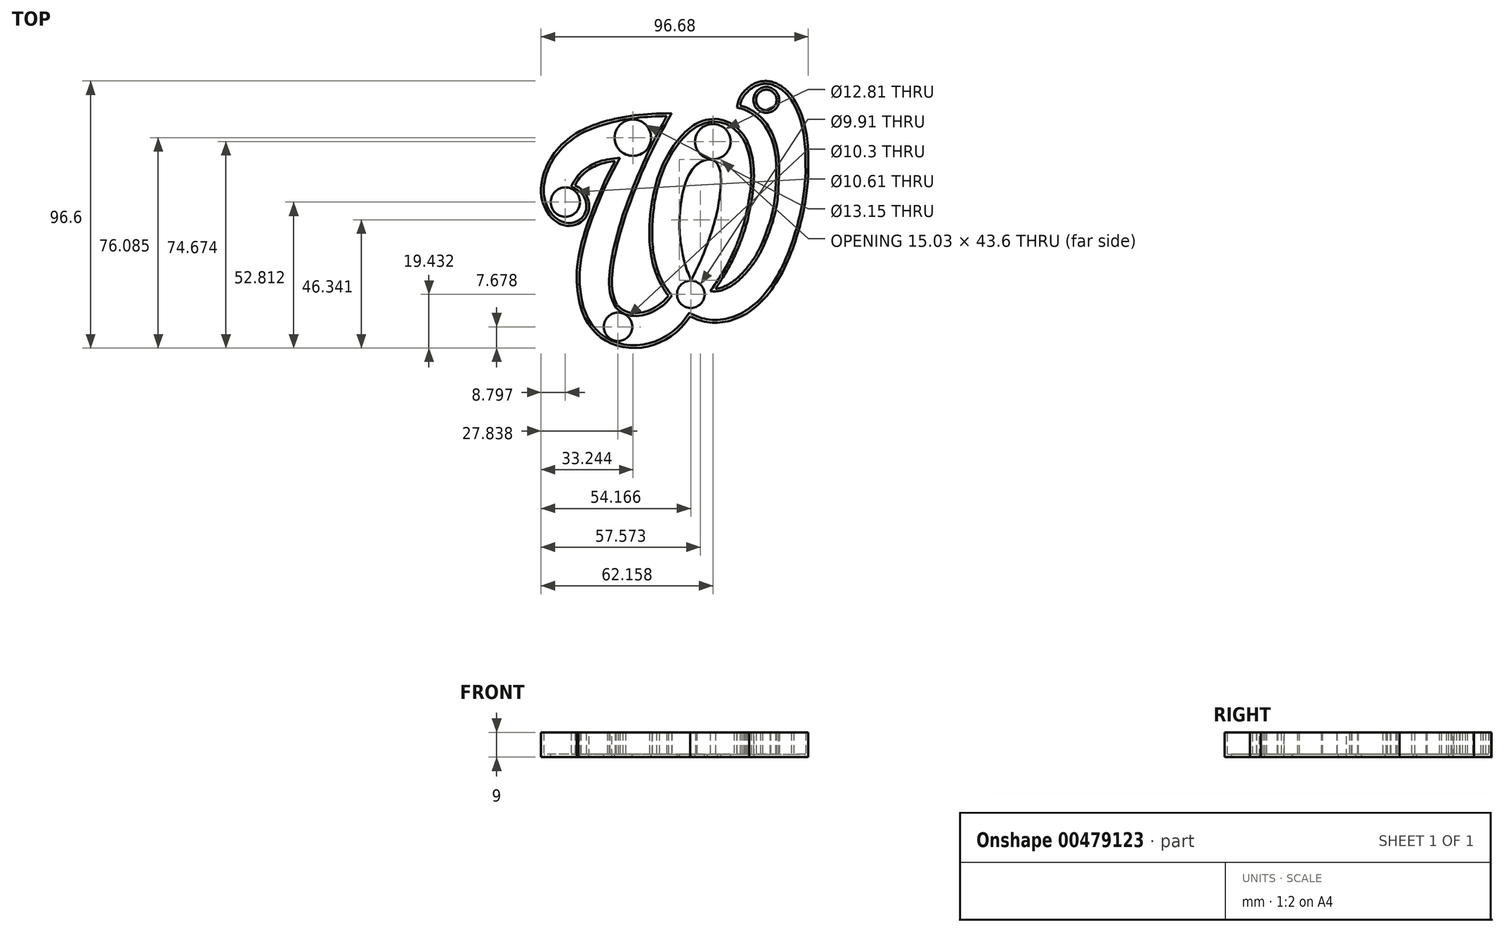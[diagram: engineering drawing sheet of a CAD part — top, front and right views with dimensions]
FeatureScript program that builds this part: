
annotation { "Feature Type Name" : "Feature", "Feature Type Description" : "" }
export const myFeature = defineFeature(function(context is Context, id is Id, definition is map)
    precondition{}
    {
        {
            var Q0;
            Q0=qCreatedBy(makeId("Top.planeOp"),FACE);
            var sketch = newSketch(context, id + "F0", { "sketchPlane" : qUnion([Q0])});
            skFitSpline(sketch, "E0", {"points": [v(-38.44, 13.04) * mm, v(-35.34, 0.5) * mm], "startDerivative": vector(19.27, -8.45) * mm, "endDerivative": vector(-8.88, -8.2) * mm});
            skFitSpline(sketch, "E1", {"points": [v(-35.34, 0.5) * mm, v(-50.32, 14.67) * mm], "startDerivative": vector(-21.62, -19.65) * mm, "endDerivative": vector(7.38, 33.62) * mm});
            skFitSpline(sketch, "E2", {"points": [v(-36.66, 32.65) * mm, v(-50.32, 14.67) * mm], "startDerivative": vector(-36.63, -20.96) * mm, "endDerivative": vector(-0.68, -3.07) * mm});
            skFitSpline(sketch, "E3", {"points": [v(-3.52, 39.1) * mm, v(-36.66, 32.65) * mm], "startDerivative": vector(-42.8, -0.12) * mm, "endDerivative": vector(-27.92, -13.6) * mm});
            skFitSpline(sketch, "E4", {"points": [v(-3.52, 39.1) * mm, v(-20.11, 2.2) * mm], "startDerivative": vector(-28.1, -51.8) * mm, "endDerivative": vector(-15.12, -41.3) * mm});
            skFitSpline(sketch, "E5", {"points": [v(-20.11, 2.2) * mm, v(-22.74, -30.6) * mm], "startDerivative": vector(-15.98, -51.16) * mm, "endDerivative": vector(11.91, -15.48) * mm});
            skFitSpline(sketch, "E6", {"points": [v(-22.74, -30.6) * mm, v(-4.6, -26.84) * mm], "startDerivative": vector(14.38, -15.94) * mm, "endDerivative": vector(11.9, 16.21) * mm});
            skFitSpline(sketch, "E7", {"points": [v(-4.6, -26.84) * mm, v(-11.49, -5.18) * mm], "startDerivative": vector(-14.06, 17.34) * mm, "endDerivative": vector(-0.4, 25.23) * mm});
            skFitSpline(sketch, "E8", {"points": [v(-8.9, 14.34) * mm, v(-11.49, -5.18) * mm], "startDerivative": vector(-7.14, -23.12) * mm, "endDerivative": vector(0.3, -10.23) * mm});
            skFitSpline(sketch, "E9", {"points": [v(5.16, 35.2) * mm, v(-8.9, 14.34) * mm], "startDerivative": vector(-12.95, -7.53) * mm, "endDerivative": vector(-9.06, -32.73) * mm});
            skFitSpline(sketch, "E10", {"points": [v(5.16, 35.2) * mm, v(24.55, 27.4) * mm], "startDerivative": vector(29.73, 16.27) * mm, "endDerivative": vector(5.54, -17.35) * mm});
            skFitSpline(sketch, "E11", {"points": [v(24.55, 27.4) * mm, v(23.9, 0) * mm], "startDerivative": vector(10, -26.88) * mm, "endDerivative": vector(-5.77, -24.7) * mm});
            skFitSpline(sketch, "E12", {"points": [v(23.9, 0) * mm, v(20.07, -10.82) * mm], "startDerivative": vector(-2.23, -7.81) * mm, "endDerivative": vector(-6.69, -15.42) * mm});
            skFitSpline(sketch, "E13", {"points": [v(12.38, -24.31) * mm, v(20.07, -10.82) * mm], "startDerivative": vector(7.85, 11.03) * mm, "endDerivative": vector(6.43, 15.26) * mm});
            skFitSpline(sketch, "E14", {"points": [v(12.38, -24.31) * mm, v(21.89, -18.84) * mm], "startDerivative": vector(9.06, -0.18) * mm, "endDerivative": vector(6.08, 7.24) * mm});
            skFitSpline(sketch, "E15", {"points": [v(29.24, -7.71) * mm, v(21.89, -18.84) * mm], "startDerivative": vector(-5.22, -12.66) * mm, "endDerivative": vector(-8.96, -9.02) * mm});
            skFitSpline(sketch, "E16", {"points": [v(34.12, 11.44) * mm, v(29.24, -7.71) * mm], "startDerivative": vector(-0.84, -23.2) * mm, "endDerivative": vector(-5.73, -13.72) * mm});
            skFitSpline(sketch, "E17", {"points": [v(28.71, 36.45) * mm, v(34.12, 11.44) * mm], "startDerivative": vector(20.5, -23.72) * mm, "endDerivative": vector(-1.25, -22.28) * mm});
            skFitSpline(sketch, "E18", {"points": [v(20.18, 41.18) * mm, v(28.71, 36.45) * mm], "startDerivative": vector(9.75, -2.02) * mm, "endDerivative": vector(8.86, -8.32) * mm});
            skFitSpline(sketch, "E19", {"points": [v(20.18, 41.18) * mm, v(23.25, 47.53) * mm], "startDerivative": vector(0.88, 6.3) * mm, "endDerivative": vector(7, 6.77) * mm});
            skFitSpline(sketch, "E20", {"points": [v(23.25, 47.53) * mm, v(32.34, 50.63) * mm], "startDerivative": vector(6.41, 6.4) * mm, "endDerivative": vector(12.36, -2.06) * mm});
            skFitSpline(sketch, "E21", {"points": [v(32.34, 50.63) * mm, v(40.68, 44.38) * mm], "startDerivative": vector(10.02, -2.32) * mm, "endDerivative": vector(5.39, -8.86) * mm});
            skFitSpline(sketch, "E22", {"points": [v(40.68, 44.38) * mm, v(45.99, 17.48) * mm], "startDerivative": vector(17.11, -26.78) * mm, "endDerivative": vector(0.17, -22.82) * mm});
            skFitSpline(sketch, "E23", {"points": [v(45.99, 17.48) * mm, v(42.24, -4.08) * mm], "startDerivative": vector(-1.45, -25.48) * mm, "endDerivative": vector(-5.86, -19.28) * mm});
            skFitSpline(sketch, "E24", {"points": [v(24.6, -32.7) * mm, v(42.24, -4.08) * mm], "startDerivative": vector(26.8, 18.38) * mm, "endDerivative": vector(10.07, 33.9) * mm});
            skFitSpline(sketch, "E25", {"points": [v(3.3, -34.32) * mm, v(24.6, -32.7) * mm], "startDerivative": vector(18.96, -10.38) * mm, "endDerivative": vector(22.17, 14.35) * mm});
            skFitSpline(sketch, "E26", {"points": [v(-37.26, -26.69) * mm, v(3.3, -34.32) * mm], "startDerivative": vector(9.1, -69.97) * mm, "endDerivative": vector(33.04, 50.98) * mm});
            skFitSpline(sketch, "E27", {"points": [v(-26.7, 16.54) * mm, v(-37.26, -26.69) * mm], "startDerivative": vector(-22.8, -49.62) * mm, "endDerivative": vector(6.72, -38.43) * mm});
            skFitSpline(sketch, "E28", {"points": [v(-23.93, 21.82) * mm, v(-26.7, 16.54) * mm], "startDerivative": vector(-2.78, -5.28) * mm, "endDerivative": vector(-2.78, -5.28) * mm});
            skFitSpline(sketch, "E29", {"points": [v(-38.44, 13.04) * mm, v(-23.93, 21.82) * mm], "startDerivative": vector(8.73, 17.34) * mm, "endDerivative": vector(18, 1.78) * mm});
            skFitSpline(sketch, "E30", {"points": [v(3.69, -18.9) * mm, v(12.08, 3.9) * mm], "startDerivative": vector(10.85, 21.47) * mm, "endDerivative": vector(5.7, 23.76) * mm});
            skFitSpline(sketch, "E31", {"points": [v(12.08, 3.9) * mm, v(9.54, 21.34) * mm], "startDerivative": vector(3.62, 18.83) * mm, "endDerivative": vector(-17.05, -2.6) * mm});
            skFitSpline(sketch, "E32", {"points": [v(0.44, -4.54) * mm, v(9.54, 21.34) * mm], "startDerivative": vector(-1.31, 24.15) * mm, "endDerivative": vector(24.76, 4.23) * mm});
            skFitSpline(sketch, "E33", {"points": [v(0.44, -4.54) * mm, v(3.69, -18.9) * mm], "startDerivative": vector(2.09, -17.75) * mm, "endDerivative": vector(5.24, -12.14) * mm});
            skCircle(sketch, "E34", {"center": v(-17.45, 30.27) * mm, "radius": 5.58 * mm});
            skCircle(sketch, "E35", {"center": v(-41.9, 7) * mm, "radius": 4.3 * mm});
            skCircle(sketch, "E36", {"center": v(-22.85, -38.13) * mm, "radius": 4.15 * mm});
            skCircle(sketch, "E37", {"center": v(3.48, -26.38) * mm, "radius": 3.96 * mm});
            skCircle(sketch, "E38", {"center": v(11.47, 28.86) * mm, "radius": 5.4 * mm});
            skCircle(sketch, "E39", {"center": v(30.8, 43.96) * mm, "radius": 3.69 * mm});
            skSolve(sketch);
        }
        {
            var Q0;
            Q0=makeQuery(id+"F0.imprint","IMPRINT",FACE,{"disambiguationData":[TD([[makeQuery(id+"F0.imprint","IMPRINT",EDGE,{"derivedFrom":sQuery(id+"F0.wireOp",EDGE,"E0")}),-1.0]])]});
            extrude(context, id + "F1", {"entities" : qUnion([Q0]), "depth" : 9 * mm});
        }
        {
            var Q0;
            Q0=makeQuery(id+"F1.opExtrude","CAP_FACE",FACE,{"disambiguationData":[OSD([sQuery(id+"F0.wireOp",EDGE,"E0"),sQuery(id+"F0.wireOp",EDGE,"E1"),sQuery(id+"F0.wireOp",EDGE,"E2"),sQuery(id+"F0.wireOp",EDGE,"E3"),sQuery(id+"F0.wireOp",EDGE,"E4"),sQuery(id+"F0.wireOp",EDGE,"E5"),sQuery(id+"F0.wireOp",EDGE,"E6"),sQuery(id+"F0.wireOp",EDGE,"E7"),sQuery(id+"F0.wireOp",EDGE,"E8"),sQuery(id+"F0.wireOp",EDGE,"E9"),sQuery(id+"F0.wireOp",EDGE,"E10"),sQuery(id+"F0.wireOp",EDGE,"E11"),sQuery(id+"F0.wireOp",EDGE,"E12"),sQuery(id+"F0.wireOp",EDGE,"E13"),sQuery(id+"F0.wireOp",EDGE,"E14"),sQuery(id+"F0.wireOp",EDGE,"E15"),sQuery(id+"F0.wireOp",EDGE,"E16"),sQuery(id+"F0.wireOp",EDGE,"E17"),sQuery(id+"F0.wireOp",EDGE,"E18"),sQuery(id+"F0.wireOp",EDGE,"E19"),sQuery(id+"F0.wireOp",EDGE,"E20"),sQuery(id+"F0.wireOp",EDGE,"E21"),sQuery(id+"F0.wireOp",EDGE,"E22"),sQuery(id+"F0.wireOp",EDGE,"E23"),sQuery(id+"F0.wireOp",EDGE,"E24"),sQuery(id+"F0.wireOp",EDGE,"E25"),sQuery(id+"F0.wireOp",EDGE,"E26"),sQuery(id+"F0.wireOp",EDGE,"E27"),sQuery(id+"F0.wireOp",EDGE,"E28"),sQuery(id+"F0.wireOp",EDGE,"E29"),sQuery(id+"F0.wireOp",EDGE,"E30"),sQuery(id+"F0.wireOp",EDGE,"E31"),sQuery(id+"F0.wireOp",EDGE,"E32"),sQuery(id+"F0.wireOp",EDGE,"E33"),sQuery(id+"F0.wireOp",EDGE,"T4ResZmE-MT7P-ZZB1-tC4J-8hycNHcue7vr"),sQuery(id+"F0.wireOp",EDGE,"OMnXbtUw-R1gw-jA70-7ST3-ESDXTdVTGBNz"),sQuery(id+"F0.wireOp",EDGE,"2kX4wL51-abr2-e3rj-M2hi-KkItlir6IYqc"),sQuery(id+"F0.wireOp",EDGE,"5Vguvqgd-1i0I-IiD5-Ilya-cWlO0dk4ybGS"),sQuery(id+"F0.wireOp",EDGE,"b57bD0nZ-s6Al-luj6-F2sP-Uw2OASkc7xh6"),sQuery(id+"F0.wireOp",EDGE,"YTZRzNyw-rSVb-fAv7-5o0Q-GydmuSaNebT5"),sQuery(id+"F0.wireOp",EDGE,"wcS51u0E-04dH-7dC1-kLtU-daWTJbN2IP2I")])],"isStart":false});
            shell(context, id + "F2", {"entities" : qUnion([Q0]), "thickness" : 1 * mm});
        }
        {
            var Q0;
            {var subQ0=sQuery(id+"F0.wireOp",EDGE,"E39");var subQ1=sQuery(id+"F0.wireOp",EDGE,"E38");var subQ2=sQuery(id+"F0.wireOp",EDGE,"E37");var subQ3=sQuery(id+"F0.wireOp",EDGE,"E36");var subQ4=sQuery(id+"F0.wireOp",EDGE,"E35");var subQ5=sQuery(id+"F0.wireOp",EDGE,"E34");var subQ6=sQuery(id+"F0.wireOp",EDGE,"E33");var subQ7=sQuery(id+"F0.wireOp",EDGE,"E32");var subQ8=sQuery(id+"F0.wireOp",EDGE,"E31");var subQ9=sQuery(id+"F0.wireOp",EDGE,"E30");var subQ10=sQuery(id+"F0.wireOp",EDGE,"E29");var subQ11=sQuery(id+"F0.wireOp",EDGE,"E28");var subQ12=sQuery(id+"F0.wireOp",EDGE,"E27");var subQ13=sQuery(id+"F0.wireOp",EDGE,"E26");var subQ14=sQuery(id+"F0.wireOp",EDGE,"E25");var subQ15=sQuery(id+"F0.wireOp",EDGE,"E24");var subQ16=sQuery(id+"F0.wireOp",EDGE,"E23");var subQ17=sQuery(id+"F0.wireOp",EDGE,"E22");var subQ18=sQuery(id+"F0.wireOp",EDGE,"E21");var subQ19=sQuery(id+"F0.wireOp",EDGE,"E20");var subQ20=sQuery(id+"F0.wireOp",EDGE,"E19");var subQ21=sQuery(id+"F0.wireOp",EDGE,"E18");var subQ22=sQuery(id+"F0.wireOp",EDGE,"E17");var subQ23=sQuery(id+"F0.wireOp",EDGE,"E16");var subQ24=sQuery(id+"F0.wireOp",EDGE,"E15");var subQ25=sQuery(id+"F0.wireOp",EDGE,"E14");var subQ26=sQuery(id+"F0.wireOp",EDGE,"E13");var subQ27=sQuery(id+"F0.wireOp",EDGE,"E12");var subQ28=sQuery(id+"F0.wireOp",EDGE,"E11");var subQ29=sQuery(id+"F0.wireOp",EDGE,"E10");var subQ30=sQuery(id+"F0.wireOp",EDGE,"E9");var subQ31=sQuery(id+"F0.wireOp",EDGE,"E8");var subQ32=sQuery(id+"F0.wireOp",EDGE,"E7");var subQ33=sQuery(id+"F0.wireOp",EDGE,"E6");var subQ34=sQuery(id+"F0.wireOp",EDGE,"E5");var subQ35=sQuery(id+"F0.wireOp",EDGE,"E4");var subQ36=sQuery(id+"F0.wireOp",EDGE,"E3");var subQ37=sQuery(id+"F0.wireOp",EDGE,"E2");var subQ38=sQuery(id+"F0.wireOp",EDGE,"E1");var subQ39=sQuery(id+"F0.wireOp",EDGE,"E0");Q0=makeQuery(id+"F2.opShell","OFFSET_FACE",FACE,{"disambiguationData":[OSD([subQ39,subQ38,subQ37,subQ36,subQ35,subQ34,subQ33,subQ32,subQ31,subQ30,subQ29,subQ28,subQ27,subQ26,subQ25,subQ24,subQ23,subQ22,subQ21,subQ20,subQ19,subQ18,subQ17,subQ16,subQ15,subQ14,subQ13,subQ12,subQ11,subQ10,subQ9,subQ8,subQ7,subQ6,subQ5,subQ4,subQ3,subQ2,subQ1,subQ0]),TDD([makeQuery(id+"F1.opExtrude","CAP_FACE",FACE,{"disambiguationData":[OSD([subQ39,subQ38,subQ37,subQ36,subQ35,subQ34,subQ33,subQ32,subQ31,subQ30,subQ29,subQ28,subQ27,subQ26,subQ25,subQ24,subQ23,subQ22,subQ21,subQ20,subQ19,subQ18,subQ17,subQ16,subQ15,subQ14,subQ13,subQ12,subQ11,subQ10,subQ9,subQ8,subQ7,subQ6,subQ5,subQ4,subQ3,subQ2,subQ1,subQ0])],"isStart":false})]),OD(1.0)]});}
            var Q1;
            {var subQ0=sQuery(id+"F0.wireOp",EDGE,"E39");var subQ1=sQuery(id+"F0.wireOp",EDGE,"E38");var subQ2=sQuery(id+"F0.wireOp",EDGE,"E37");var subQ3=sQuery(id+"F0.wireOp",EDGE,"E36");var subQ4=sQuery(id+"F0.wireOp",EDGE,"E35");var subQ5=sQuery(id+"F0.wireOp",EDGE,"E34");var subQ6=sQuery(id+"F0.wireOp",EDGE,"E33");var subQ7=sQuery(id+"F0.wireOp",EDGE,"E32");var subQ8=sQuery(id+"F0.wireOp",EDGE,"E31");var subQ9=sQuery(id+"F0.wireOp",EDGE,"E30");var subQ10=sQuery(id+"F0.wireOp",EDGE,"E29");var subQ11=sQuery(id+"F0.wireOp",EDGE,"E28");var subQ12=sQuery(id+"F0.wireOp",EDGE,"E27");var subQ13=sQuery(id+"F0.wireOp",EDGE,"E26");var subQ14=sQuery(id+"F0.wireOp",EDGE,"E25");var subQ15=sQuery(id+"F0.wireOp",EDGE,"E24");var subQ16=sQuery(id+"F0.wireOp",EDGE,"E23");var subQ17=sQuery(id+"F0.wireOp",EDGE,"E22");var subQ18=sQuery(id+"F0.wireOp",EDGE,"E21");var subQ19=sQuery(id+"F0.wireOp",EDGE,"E20");var subQ20=sQuery(id+"F0.wireOp",EDGE,"E19");var subQ21=sQuery(id+"F0.wireOp",EDGE,"E18");var subQ22=sQuery(id+"F0.wireOp",EDGE,"E17");var subQ23=sQuery(id+"F0.wireOp",EDGE,"E16");var subQ24=sQuery(id+"F0.wireOp",EDGE,"E15");var subQ25=sQuery(id+"F0.wireOp",EDGE,"E14");var subQ26=sQuery(id+"F0.wireOp",EDGE,"E13");var subQ27=sQuery(id+"F0.wireOp",EDGE,"E12");var subQ28=sQuery(id+"F0.wireOp",EDGE,"E11");var subQ29=sQuery(id+"F0.wireOp",EDGE,"E10");var subQ30=sQuery(id+"F0.wireOp",EDGE,"E9");var subQ31=sQuery(id+"F0.wireOp",EDGE,"E8");var subQ32=sQuery(id+"F0.wireOp",EDGE,"E7");var subQ33=sQuery(id+"F0.wireOp",EDGE,"E6");var subQ34=sQuery(id+"F0.wireOp",EDGE,"E5");var subQ35=sQuery(id+"F0.wireOp",EDGE,"E4");var subQ36=sQuery(id+"F0.wireOp",EDGE,"E3");var subQ37=sQuery(id+"F0.wireOp",EDGE,"E2");var subQ38=sQuery(id+"F0.wireOp",EDGE,"E1");var subQ39=sQuery(id+"F0.wireOp",EDGE,"E0");Q1=makeQuery(id+"F2.opShell","OFFSET_FACE",FACE,{"disambiguationData":[OSD([subQ39,subQ38,subQ37,subQ36,subQ35,subQ34,subQ33,subQ32,subQ31,subQ30,subQ29,subQ28,subQ27,subQ26,subQ25,subQ24,subQ23,subQ22,subQ21,subQ20,subQ19,subQ18,subQ17,subQ16,subQ15,subQ14,subQ13,subQ12,subQ11,subQ10,subQ9,subQ8,subQ7,subQ6,subQ5,subQ4,subQ3,subQ2,subQ1,subQ0]),TDD([makeQuery(id+"F1.opExtrude","CAP_FACE",FACE,{"disambiguationData":[OSD([subQ39,subQ38,subQ37,subQ36,subQ35,subQ34,subQ33,subQ32,subQ31,subQ30,subQ29,subQ28,subQ27,subQ26,subQ25,subQ24,subQ23,subQ22,subQ21,subQ20,subQ19,subQ18,subQ17,subQ16,subQ15,subQ14,subQ13,subQ12,subQ11,subQ10,subQ9,subQ8,subQ7,subQ6,subQ5,subQ4,subQ3,subQ2,subQ1,subQ0])],"isStart":false})]),OD(2.0)]});}
            var Q2;
            {var subQ0=sQuery(id+"F0.wireOp",EDGE,"E39");var subQ1=sQuery(id+"F0.wireOp",EDGE,"E38");var subQ2=sQuery(id+"F0.wireOp",EDGE,"E37");var subQ3=sQuery(id+"F0.wireOp",EDGE,"E36");var subQ4=sQuery(id+"F0.wireOp",EDGE,"E35");var subQ5=sQuery(id+"F0.wireOp",EDGE,"E34");var subQ6=sQuery(id+"F0.wireOp",EDGE,"E33");var subQ7=sQuery(id+"F0.wireOp",EDGE,"E32");var subQ8=sQuery(id+"F0.wireOp",EDGE,"E31");var subQ9=sQuery(id+"F0.wireOp",EDGE,"E30");var subQ10=sQuery(id+"F0.wireOp",EDGE,"E29");var subQ11=sQuery(id+"F0.wireOp",EDGE,"E28");var subQ12=sQuery(id+"F0.wireOp",EDGE,"E27");var subQ13=sQuery(id+"F0.wireOp",EDGE,"E26");var subQ14=sQuery(id+"F0.wireOp",EDGE,"E25");var subQ15=sQuery(id+"F0.wireOp",EDGE,"E24");var subQ16=sQuery(id+"F0.wireOp",EDGE,"E23");var subQ17=sQuery(id+"F0.wireOp",EDGE,"E22");var subQ18=sQuery(id+"F0.wireOp",EDGE,"E21");var subQ19=sQuery(id+"F0.wireOp",EDGE,"E20");var subQ20=sQuery(id+"F0.wireOp",EDGE,"E19");var subQ21=sQuery(id+"F0.wireOp",EDGE,"E18");var subQ22=sQuery(id+"F0.wireOp",EDGE,"E17");var subQ23=sQuery(id+"F0.wireOp",EDGE,"E16");var subQ24=sQuery(id+"F0.wireOp",EDGE,"E15");var subQ25=sQuery(id+"F0.wireOp",EDGE,"E14");var subQ26=sQuery(id+"F0.wireOp",EDGE,"E13");var subQ27=sQuery(id+"F0.wireOp",EDGE,"E12");var subQ28=sQuery(id+"F0.wireOp",EDGE,"E11");var subQ29=sQuery(id+"F0.wireOp",EDGE,"E10");var subQ30=sQuery(id+"F0.wireOp",EDGE,"E9");var subQ31=sQuery(id+"F0.wireOp",EDGE,"E8");var subQ32=sQuery(id+"F0.wireOp",EDGE,"E7");var subQ33=sQuery(id+"F0.wireOp",EDGE,"E6");var subQ34=sQuery(id+"F0.wireOp",EDGE,"E5");var subQ35=sQuery(id+"F0.wireOp",EDGE,"E4");var subQ36=sQuery(id+"F0.wireOp",EDGE,"E3");var subQ37=sQuery(id+"F0.wireOp",EDGE,"E2");var subQ38=sQuery(id+"F0.wireOp",EDGE,"E1");var subQ39=sQuery(id+"F0.wireOp",EDGE,"E0");Q2=makeQuery(id+"F2.opShell","OFFSET_FACE",FACE,{"disambiguationData":[OSD([subQ39,subQ38,subQ37,subQ36,subQ35,subQ34,subQ33,subQ32,subQ31,subQ30,subQ29,subQ28,subQ27,subQ26,subQ25,subQ24,subQ23,subQ22,subQ21,subQ20,subQ19,subQ18,subQ17,subQ16,subQ15,subQ14,subQ13,subQ12,subQ11,subQ10,subQ9,subQ8,subQ7,subQ6,subQ5,subQ4,subQ3,subQ2,subQ1,subQ0]),TDD([makeQuery(id+"F1.opExtrude","CAP_FACE",FACE,{"disambiguationData":[OSD([subQ39,subQ38,subQ37,subQ36,subQ35,subQ34,subQ33,subQ32,subQ31,subQ30,subQ29,subQ28,subQ27,subQ26,subQ25,subQ24,subQ23,subQ22,subQ21,subQ20,subQ19,subQ18,subQ17,subQ16,subQ15,subQ14,subQ13,subQ12,subQ11,subQ10,subQ9,subQ8,subQ7,subQ6,subQ5,subQ4,subQ3,subQ2,subQ1,subQ0])],"isStart":false})]),OD(3.0)]});}
            var Q3;
            {var subQ0=sQuery(id+"F0.wireOp",EDGE,"E39");var subQ1=sQuery(id+"F0.wireOp",EDGE,"E38");var subQ2=sQuery(id+"F0.wireOp",EDGE,"E37");var subQ3=sQuery(id+"F0.wireOp",EDGE,"E36");var subQ4=sQuery(id+"F0.wireOp",EDGE,"E35");var subQ5=sQuery(id+"F0.wireOp",EDGE,"E34");var subQ6=sQuery(id+"F0.wireOp",EDGE,"E33");var subQ7=sQuery(id+"F0.wireOp",EDGE,"E32");var subQ8=sQuery(id+"F0.wireOp",EDGE,"E31");var subQ9=sQuery(id+"F0.wireOp",EDGE,"E30");var subQ10=sQuery(id+"F0.wireOp",EDGE,"E29");var subQ11=sQuery(id+"F0.wireOp",EDGE,"E28");var subQ12=sQuery(id+"F0.wireOp",EDGE,"E27");var subQ13=sQuery(id+"F0.wireOp",EDGE,"E26");var subQ14=sQuery(id+"F0.wireOp",EDGE,"E25");var subQ15=sQuery(id+"F0.wireOp",EDGE,"E24");var subQ16=sQuery(id+"F0.wireOp",EDGE,"E23");var subQ17=sQuery(id+"F0.wireOp",EDGE,"E22");var subQ18=sQuery(id+"F0.wireOp",EDGE,"E21");var subQ19=sQuery(id+"F0.wireOp",EDGE,"E20");var subQ20=sQuery(id+"F0.wireOp",EDGE,"E19");var subQ21=sQuery(id+"F0.wireOp",EDGE,"E18");var subQ22=sQuery(id+"F0.wireOp",EDGE,"E17");var subQ23=sQuery(id+"F0.wireOp",EDGE,"E16");var subQ24=sQuery(id+"F0.wireOp",EDGE,"E15");var subQ25=sQuery(id+"F0.wireOp",EDGE,"E14");var subQ26=sQuery(id+"F0.wireOp",EDGE,"E13");var subQ27=sQuery(id+"F0.wireOp",EDGE,"E12");var subQ28=sQuery(id+"F0.wireOp",EDGE,"E11");var subQ29=sQuery(id+"F0.wireOp",EDGE,"E10");var subQ30=sQuery(id+"F0.wireOp",EDGE,"E9");var subQ31=sQuery(id+"F0.wireOp",EDGE,"E8");var subQ32=sQuery(id+"F0.wireOp",EDGE,"E7");var subQ33=sQuery(id+"F0.wireOp",EDGE,"E6");var subQ34=sQuery(id+"F0.wireOp",EDGE,"E5");var subQ35=sQuery(id+"F0.wireOp",EDGE,"E4");var subQ36=sQuery(id+"F0.wireOp",EDGE,"E3");var subQ37=sQuery(id+"F0.wireOp",EDGE,"E2");var subQ38=sQuery(id+"F0.wireOp",EDGE,"E1");var subQ39=sQuery(id+"F0.wireOp",EDGE,"E0");Q3=makeQuery(id+"F2.opShell","OFFSET_FACE",FACE,{"disambiguationData":[OSD([subQ39,subQ38,subQ37,subQ36,subQ35,subQ34,subQ33,subQ32,subQ31,subQ30,subQ29,subQ28,subQ27,subQ26,subQ25,subQ24,subQ23,subQ22,subQ21,subQ20,subQ19,subQ18,subQ17,subQ16,subQ15,subQ14,subQ13,subQ12,subQ11,subQ10,subQ9,subQ8,subQ7,subQ6,subQ5,subQ4,subQ3,subQ2,subQ1,subQ0]),TDD([makeQuery(id+"F1.opExtrude","CAP_FACE",FACE,{"disambiguationData":[OSD([subQ39,subQ38,subQ37,subQ36,subQ35,subQ34,subQ33,subQ32,subQ31,subQ30,subQ29,subQ28,subQ27,subQ26,subQ25,subQ24,subQ23,subQ22,subQ21,subQ20,subQ19,subQ18,subQ17,subQ16,subQ15,subQ14,subQ13,subQ12,subQ11,subQ10,subQ9,subQ8,subQ7,subQ6,subQ5,subQ4,subQ3,subQ2,subQ1,subQ0])],"isStart":false})]),OD(4.0)]});}
            var Q4;
            {var subQ0=sQuery(id+"F0.wireOp",EDGE,"E39");var subQ1=sQuery(id+"F0.wireOp",EDGE,"E38");var subQ2=sQuery(id+"F0.wireOp",EDGE,"E37");var subQ3=sQuery(id+"F0.wireOp",EDGE,"E36");var subQ4=sQuery(id+"F0.wireOp",EDGE,"E35");var subQ5=sQuery(id+"F0.wireOp",EDGE,"E34");var subQ6=sQuery(id+"F0.wireOp",EDGE,"E33");var subQ7=sQuery(id+"F0.wireOp",EDGE,"E32");var subQ8=sQuery(id+"F0.wireOp",EDGE,"E31");var subQ9=sQuery(id+"F0.wireOp",EDGE,"E30");var subQ10=sQuery(id+"F0.wireOp",EDGE,"E29");var subQ11=sQuery(id+"F0.wireOp",EDGE,"E28");var subQ12=sQuery(id+"F0.wireOp",EDGE,"E27");var subQ13=sQuery(id+"F0.wireOp",EDGE,"E26");var subQ14=sQuery(id+"F0.wireOp",EDGE,"E25");var subQ15=sQuery(id+"F0.wireOp",EDGE,"E24");var subQ16=sQuery(id+"F0.wireOp",EDGE,"E23");var subQ17=sQuery(id+"F0.wireOp",EDGE,"E22");var subQ18=sQuery(id+"F0.wireOp",EDGE,"E21");var subQ19=sQuery(id+"F0.wireOp",EDGE,"E20");var subQ20=sQuery(id+"F0.wireOp",EDGE,"E19");var subQ21=sQuery(id+"F0.wireOp",EDGE,"E18");var subQ22=sQuery(id+"F0.wireOp",EDGE,"E17");var subQ23=sQuery(id+"F0.wireOp",EDGE,"E16");var subQ24=sQuery(id+"F0.wireOp",EDGE,"E15");var subQ25=sQuery(id+"F0.wireOp",EDGE,"E14");var subQ26=sQuery(id+"F0.wireOp",EDGE,"E13");var subQ27=sQuery(id+"F0.wireOp",EDGE,"E12");var subQ28=sQuery(id+"F0.wireOp",EDGE,"E11");var subQ29=sQuery(id+"F0.wireOp",EDGE,"E10");var subQ30=sQuery(id+"F0.wireOp",EDGE,"E9");var subQ31=sQuery(id+"F0.wireOp",EDGE,"E8");var subQ32=sQuery(id+"F0.wireOp",EDGE,"E7");var subQ33=sQuery(id+"F0.wireOp",EDGE,"E6");var subQ34=sQuery(id+"F0.wireOp",EDGE,"E5");var subQ35=sQuery(id+"F0.wireOp",EDGE,"E4");var subQ36=sQuery(id+"F0.wireOp",EDGE,"E3");var subQ37=sQuery(id+"F0.wireOp",EDGE,"E2");var subQ38=sQuery(id+"F0.wireOp",EDGE,"E1");var subQ39=sQuery(id+"F0.wireOp",EDGE,"E0");Q4=makeQuery(id+"F2.opShell","OFFSET_FACE",FACE,{"disambiguationData":[OSD([subQ39,subQ38,subQ37,subQ36,subQ35,subQ34,subQ33,subQ32,subQ31,subQ30,subQ29,subQ28,subQ27,subQ26,subQ25,subQ24,subQ23,subQ22,subQ21,subQ20,subQ19,subQ18,subQ17,subQ16,subQ15,subQ14,subQ13,subQ12,subQ11,subQ10,subQ9,subQ8,subQ7,subQ6,subQ5,subQ4,subQ3,subQ2,subQ1,subQ0]),TDD([makeQuery(id+"F1.opExtrude","CAP_FACE",FACE,{"disambiguationData":[OSD([subQ39,subQ38,subQ37,subQ36,subQ35,subQ34,subQ33,subQ32,subQ31,subQ30,subQ29,subQ28,subQ27,subQ26,subQ25,subQ24,subQ23,subQ22,subQ21,subQ20,subQ19,subQ18,subQ17,subQ16,subQ15,subQ14,subQ13,subQ12,subQ11,subQ10,subQ9,subQ8,subQ7,subQ6,subQ5,subQ4,subQ3,subQ2,subQ1,subQ0])],"isStart":false})]),OD(5.0)]});}
            var Q5;
            {var subQ0=sQuery(id+"F0.wireOp",EDGE,"E39");var subQ1=sQuery(id+"F0.wireOp",EDGE,"E38");var subQ2=sQuery(id+"F0.wireOp",EDGE,"E37");var subQ3=sQuery(id+"F0.wireOp",EDGE,"E36");var subQ4=sQuery(id+"F0.wireOp",EDGE,"E35");var subQ5=sQuery(id+"F0.wireOp",EDGE,"E34");var subQ6=sQuery(id+"F0.wireOp",EDGE,"E33");var subQ7=sQuery(id+"F0.wireOp",EDGE,"E32");var subQ8=sQuery(id+"F0.wireOp",EDGE,"E31");var subQ9=sQuery(id+"F0.wireOp",EDGE,"E30");var subQ10=sQuery(id+"F0.wireOp",EDGE,"E29");var subQ11=sQuery(id+"F0.wireOp",EDGE,"E28");var subQ12=sQuery(id+"F0.wireOp",EDGE,"E27");var subQ13=sQuery(id+"F0.wireOp",EDGE,"E26");var subQ14=sQuery(id+"F0.wireOp",EDGE,"E25");var subQ15=sQuery(id+"F0.wireOp",EDGE,"E24");var subQ16=sQuery(id+"F0.wireOp",EDGE,"E23");var subQ17=sQuery(id+"F0.wireOp",EDGE,"E22");var subQ18=sQuery(id+"F0.wireOp",EDGE,"E21");var subQ19=sQuery(id+"F0.wireOp",EDGE,"E20");var subQ20=sQuery(id+"F0.wireOp",EDGE,"E19");var subQ21=sQuery(id+"F0.wireOp",EDGE,"E18");var subQ22=sQuery(id+"F0.wireOp",EDGE,"E17");var subQ23=sQuery(id+"F0.wireOp",EDGE,"E16");var subQ24=sQuery(id+"F0.wireOp",EDGE,"E15");var subQ25=sQuery(id+"F0.wireOp",EDGE,"E14");var subQ26=sQuery(id+"F0.wireOp",EDGE,"E13");var subQ27=sQuery(id+"F0.wireOp",EDGE,"E12");var subQ28=sQuery(id+"F0.wireOp",EDGE,"E11");var subQ29=sQuery(id+"F0.wireOp",EDGE,"E10");var subQ30=sQuery(id+"F0.wireOp",EDGE,"E9");var subQ31=sQuery(id+"F0.wireOp",EDGE,"E8");var subQ32=sQuery(id+"F0.wireOp",EDGE,"E7");var subQ33=sQuery(id+"F0.wireOp",EDGE,"E6");var subQ34=sQuery(id+"F0.wireOp",EDGE,"E5");var subQ35=sQuery(id+"F0.wireOp",EDGE,"E4");var subQ36=sQuery(id+"F0.wireOp",EDGE,"E3");var subQ37=sQuery(id+"F0.wireOp",EDGE,"E2");var subQ38=sQuery(id+"F0.wireOp",EDGE,"E1");var subQ39=sQuery(id+"F0.wireOp",EDGE,"E0");Q5=makeQuery(id+"F2.opShell","OFFSET_FACE",FACE,{"disambiguationData":[OSD([subQ39,subQ38,subQ37,subQ36,subQ35,subQ34,subQ33,subQ32,subQ31,subQ30,subQ29,subQ28,subQ27,subQ26,subQ25,subQ24,subQ23,subQ22,subQ21,subQ20,subQ19,subQ18,subQ17,subQ16,subQ15,subQ14,subQ13,subQ12,subQ11,subQ10,subQ9,subQ8,subQ7,subQ6,subQ5,subQ4,subQ3,subQ2,subQ1,subQ0]),TDD([makeQuery(id+"F1.opExtrude","CAP_FACE",FACE,{"disambiguationData":[OSD([subQ39,subQ38,subQ37,subQ36,subQ35,subQ34,subQ33,subQ32,subQ31,subQ30,subQ29,subQ28,subQ27,subQ26,subQ25,subQ24,subQ23,subQ22,subQ21,subQ20,subQ19,subQ18,subQ17,subQ16,subQ15,subQ14,subQ13,subQ12,subQ11,subQ10,subQ9,subQ8,subQ7,subQ6,subQ5,subQ4,subQ3,subQ2,subQ1,subQ0])],"isStart":false})]),OD(3.0)]});}
            var Q6;
            {var subQ0=sQuery(id+"F0.wireOp",EDGE,"E39");var subQ1=sQuery(id+"F0.wireOp",EDGE,"E38");var subQ2=sQuery(id+"F0.wireOp",EDGE,"E37");var subQ3=sQuery(id+"F0.wireOp",EDGE,"E36");var subQ4=sQuery(id+"F0.wireOp",EDGE,"E35");var subQ5=sQuery(id+"F0.wireOp",EDGE,"E34");var subQ6=sQuery(id+"F0.wireOp",EDGE,"E33");var subQ7=sQuery(id+"F0.wireOp",EDGE,"E32");var subQ8=sQuery(id+"F0.wireOp",EDGE,"E31");var subQ9=sQuery(id+"F0.wireOp",EDGE,"E30");var subQ10=sQuery(id+"F0.wireOp",EDGE,"E29");var subQ11=sQuery(id+"F0.wireOp",EDGE,"E28");var subQ12=sQuery(id+"F0.wireOp",EDGE,"E27");var subQ13=sQuery(id+"F0.wireOp",EDGE,"E26");var subQ14=sQuery(id+"F0.wireOp",EDGE,"E25");var subQ15=sQuery(id+"F0.wireOp",EDGE,"E24");var subQ16=sQuery(id+"F0.wireOp",EDGE,"E23");var subQ17=sQuery(id+"F0.wireOp",EDGE,"E22");var subQ18=sQuery(id+"F0.wireOp",EDGE,"E21");var subQ19=sQuery(id+"F0.wireOp",EDGE,"E20");var subQ20=sQuery(id+"F0.wireOp",EDGE,"E19");var subQ21=sQuery(id+"F0.wireOp",EDGE,"E18");var subQ22=sQuery(id+"F0.wireOp",EDGE,"E17");var subQ23=sQuery(id+"F0.wireOp",EDGE,"E16");var subQ24=sQuery(id+"F0.wireOp",EDGE,"E15");var subQ25=sQuery(id+"F0.wireOp",EDGE,"E14");var subQ26=sQuery(id+"F0.wireOp",EDGE,"E13");var subQ27=sQuery(id+"F0.wireOp",EDGE,"E12");var subQ28=sQuery(id+"F0.wireOp",EDGE,"E11");var subQ29=sQuery(id+"F0.wireOp",EDGE,"E10");var subQ30=sQuery(id+"F0.wireOp",EDGE,"E9");var subQ31=sQuery(id+"F0.wireOp",EDGE,"E8");var subQ32=sQuery(id+"F0.wireOp",EDGE,"E7");var subQ33=sQuery(id+"F0.wireOp",EDGE,"E6");var subQ34=sQuery(id+"F0.wireOp",EDGE,"E5");var subQ35=sQuery(id+"F0.wireOp",EDGE,"E4");var subQ36=sQuery(id+"F0.wireOp",EDGE,"E3");var subQ37=sQuery(id+"F0.wireOp",EDGE,"E2");var subQ38=sQuery(id+"F0.wireOp",EDGE,"E1");var subQ39=sQuery(id+"F0.wireOp",EDGE,"E0");Q6=makeQuery(id+"F2.opShell","OFFSET_FACE",FACE,{"disambiguationData":[OSD([subQ39,subQ38,subQ37,subQ36,subQ35,subQ34,subQ33,subQ32,subQ31,subQ30,subQ29,subQ28,subQ27,subQ26,subQ25,subQ24,subQ23,subQ22,subQ21,subQ20,subQ19,subQ18,subQ17,subQ16,subQ15,subQ14,subQ13,subQ12,subQ11,subQ10,subQ9,subQ8,subQ7,subQ6,subQ5,subQ4,subQ3,subQ2,subQ1,subQ0]),TDD([makeQuery(id+"F1.opExtrude","CAP_FACE",FACE,{"disambiguationData":[OSD([subQ39,subQ38,subQ37,subQ36,subQ35,subQ34,subQ33,subQ32,subQ31,subQ30,subQ29,subQ28,subQ27,subQ26,subQ25,subQ24,subQ23,subQ22,subQ21,subQ20,subQ19,subQ18,subQ17,subQ16,subQ15,subQ14,subQ13,subQ12,subQ11,subQ10,subQ9,subQ8,subQ7,subQ6,subQ5,subQ4,subQ3,subQ2,subQ1,subQ0])],"isStart":false})]),OD(4.0)]});}
            var Q7;
            {var subQ0=sQuery(id+"F0.wireOp",EDGE,"E39");var subQ1=sQuery(id+"F0.wireOp",EDGE,"E38");var subQ2=sQuery(id+"F0.wireOp",EDGE,"E37");var subQ3=sQuery(id+"F0.wireOp",EDGE,"E36");var subQ4=sQuery(id+"F0.wireOp",EDGE,"E35");var subQ5=sQuery(id+"F0.wireOp",EDGE,"E34");var subQ6=sQuery(id+"F0.wireOp",EDGE,"E33");var subQ7=sQuery(id+"F0.wireOp",EDGE,"E32");var subQ8=sQuery(id+"F0.wireOp",EDGE,"E31");var subQ9=sQuery(id+"F0.wireOp",EDGE,"E30");var subQ10=sQuery(id+"F0.wireOp",EDGE,"E29");var subQ11=sQuery(id+"F0.wireOp",EDGE,"E28");var subQ12=sQuery(id+"F0.wireOp",EDGE,"E27");var subQ13=sQuery(id+"F0.wireOp",EDGE,"E26");var subQ14=sQuery(id+"F0.wireOp",EDGE,"E25");var subQ15=sQuery(id+"F0.wireOp",EDGE,"E24");var subQ16=sQuery(id+"F0.wireOp",EDGE,"E23");var subQ17=sQuery(id+"F0.wireOp",EDGE,"E22");var subQ18=sQuery(id+"F0.wireOp",EDGE,"E21");var subQ19=sQuery(id+"F0.wireOp",EDGE,"E20");var subQ20=sQuery(id+"F0.wireOp",EDGE,"E19");var subQ21=sQuery(id+"F0.wireOp",EDGE,"E18");var subQ22=sQuery(id+"F0.wireOp",EDGE,"E17");var subQ23=sQuery(id+"F0.wireOp",EDGE,"E16");var subQ24=sQuery(id+"F0.wireOp",EDGE,"E15");var subQ25=sQuery(id+"F0.wireOp",EDGE,"E14");var subQ26=sQuery(id+"F0.wireOp",EDGE,"E13");var subQ27=sQuery(id+"F0.wireOp",EDGE,"E12");var subQ28=sQuery(id+"F0.wireOp",EDGE,"E11");var subQ29=sQuery(id+"F0.wireOp",EDGE,"E10");var subQ30=sQuery(id+"F0.wireOp",EDGE,"E9");var subQ31=sQuery(id+"F0.wireOp",EDGE,"E8");var subQ32=sQuery(id+"F0.wireOp",EDGE,"E7");var subQ33=sQuery(id+"F0.wireOp",EDGE,"E6");var subQ34=sQuery(id+"F0.wireOp",EDGE,"E5");var subQ35=sQuery(id+"F0.wireOp",EDGE,"E4");var subQ36=sQuery(id+"F0.wireOp",EDGE,"E3");var subQ37=sQuery(id+"F0.wireOp",EDGE,"E2");var subQ38=sQuery(id+"F0.wireOp",EDGE,"E1");var subQ39=sQuery(id+"F0.wireOp",EDGE,"E0");Q7=makeQuery(id+"F2.opShell","OFFSET_FACE",FACE,{"disambiguationData":[OSD([subQ39,subQ38,subQ37,subQ36,subQ35,subQ34,subQ33,subQ32,subQ31,subQ30,subQ29,subQ28,subQ27,subQ26,subQ25,subQ24,subQ23,subQ22,subQ21,subQ20,subQ19,subQ18,subQ17,subQ16,subQ15,subQ14,subQ13,subQ12,subQ11,subQ10,subQ9,subQ8,subQ7,subQ6,subQ5,subQ4,subQ3,subQ2,subQ1,subQ0]),TDD([makeQuery(id+"F1.opExtrude","CAP_FACE",FACE,{"disambiguationData":[OSD([subQ39,subQ38,subQ37,subQ36,subQ35,subQ34,subQ33,subQ32,subQ31,subQ30,subQ29,subQ28,subQ27,subQ26,subQ25,subQ24,subQ23,subQ22,subQ21,subQ20,subQ19,subQ18,subQ17,subQ16,subQ15,subQ14,subQ13,subQ12,subQ11,subQ10,subQ9,subQ8,subQ7,subQ6,subQ5,subQ4,subQ3,subQ2,subQ1,subQ0])],"isStart":false})]),OD(5.0)]});}
            var Q8;
            {var subQ0=sQuery(id+"F0.wireOp",EDGE,"E39");var subQ1=sQuery(id+"F0.wireOp",EDGE,"E38");var subQ2=sQuery(id+"F0.wireOp",EDGE,"E37");var subQ3=sQuery(id+"F0.wireOp",EDGE,"E36");var subQ4=sQuery(id+"F0.wireOp",EDGE,"E35");var subQ5=sQuery(id+"F0.wireOp",EDGE,"E34");var subQ6=sQuery(id+"F0.wireOp",EDGE,"E33");var subQ7=sQuery(id+"F0.wireOp",EDGE,"E32");var subQ8=sQuery(id+"F0.wireOp",EDGE,"E31");var subQ9=sQuery(id+"F0.wireOp",EDGE,"E30");var subQ10=sQuery(id+"F0.wireOp",EDGE,"E29");var subQ11=sQuery(id+"F0.wireOp",EDGE,"E28");var subQ12=sQuery(id+"F0.wireOp",EDGE,"E27");var subQ13=sQuery(id+"F0.wireOp",EDGE,"E26");var subQ14=sQuery(id+"F0.wireOp",EDGE,"E25");var subQ15=sQuery(id+"F0.wireOp",EDGE,"E24");var subQ16=sQuery(id+"F0.wireOp",EDGE,"E23");var subQ17=sQuery(id+"F0.wireOp",EDGE,"E22");var subQ18=sQuery(id+"F0.wireOp",EDGE,"E21");var subQ19=sQuery(id+"F0.wireOp",EDGE,"E20");var subQ20=sQuery(id+"F0.wireOp",EDGE,"E19");var subQ21=sQuery(id+"F0.wireOp",EDGE,"E18");var subQ22=sQuery(id+"F0.wireOp",EDGE,"E17");var subQ23=sQuery(id+"F0.wireOp",EDGE,"E16");var subQ24=sQuery(id+"F0.wireOp",EDGE,"E15");var subQ25=sQuery(id+"F0.wireOp",EDGE,"E14");var subQ26=sQuery(id+"F0.wireOp",EDGE,"E13");var subQ27=sQuery(id+"F0.wireOp",EDGE,"E12");var subQ28=sQuery(id+"F0.wireOp",EDGE,"E11");var subQ29=sQuery(id+"F0.wireOp",EDGE,"E10");var subQ30=sQuery(id+"F0.wireOp",EDGE,"E9");var subQ31=sQuery(id+"F0.wireOp",EDGE,"E8");var subQ32=sQuery(id+"F0.wireOp",EDGE,"E7");var subQ33=sQuery(id+"F0.wireOp",EDGE,"E6");var subQ34=sQuery(id+"F0.wireOp",EDGE,"E5");var subQ35=sQuery(id+"F0.wireOp",EDGE,"E4");var subQ36=sQuery(id+"F0.wireOp",EDGE,"E3");var subQ37=sQuery(id+"F0.wireOp",EDGE,"E2");var subQ38=sQuery(id+"F0.wireOp",EDGE,"E1");var subQ39=sQuery(id+"F0.wireOp",EDGE,"E0");Q8=makeQuery(id+"F2.opShell","OFFSET_FACE",FACE,{"disambiguationData":[OSD([subQ39,subQ38,subQ37,subQ36,subQ35,subQ34,subQ33,subQ32,subQ31,subQ30,subQ29,subQ28,subQ27,subQ26,subQ25,subQ24,subQ23,subQ22,subQ21,subQ20,subQ19,subQ18,subQ17,subQ16,subQ15,subQ14,subQ13,subQ12,subQ11,subQ10,subQ9,subQ8,subQ7,subQ6,subQ5,subQ4,subQ3,subQ2,subQ1,subQ0]),TDD([makeQuery(id+"F1.opExtrude","CAP_FACE",FACE,{"disambiguationData":[OSD([subQ39,subQ38,subQ37,subQ36,subQ35,subQ34,subQ33,subQ32,subQ31,subQ30,subQ29,subQ28,subQ27,subQ26,subQ25,subQ24,subQ23,subQ22,subQ21,subQ20,subQ19,subQ18,subQ17,subQ16,subQ15,subQ14,subQ13,subQ12,subQ11,subQ10,subQ9,subQ8,subQ7,subQ6,subQ5,subQ4,subQ3,subQ2,subQ1,subQ0])],"isStart":false})]),OD(1.0)]});}
            var Q9;
            {var subQ0=sQuery(id+"F0.wireOp",EDGE,"E39");var subQ1=sQuery(id+"F0.wireOp",EDGE,"E38");var subQ2=sQuery(id+"F0.wireOp",EDGE,"E37");var subQ3=sQuery(id+"F0.wireOp",EDGE,"E36");var subQ4=sQuery(id+"F0.wireOp",EDGE,"E35");var subQ5=sQuery(id+"F0.wireOp",EDGE,"E34");var subQ6=sQuery(id+"F0.wireOp",EDGE,"E33");var subQ7=sQuery(id+"F0.wireOp",EDGE,"E32");var subQ8=sQuery(id+"F0.wireOp",EDGE,"E31");var subQ9=sQuery(id+"F0.wireOp",EDGE,"E30");var subQ10=sQuery(id+"F0.wireOp",EDGE,"E29");var subQ11=sQuery(id+"F0.wireOp",EDGE,"E28");var subQ12=sQuery(id+"F0.wireOp",EDGE,"E27");var subQ13=sQuery(id+"F0.wireOp",EDGE,"E26");var subQ14=sQuery(id+"F0.wireOp",EDGE,"E25");var subQ15=sQuery(id+"F0.wireOp",EDGE,"E24");var subQ16=sQuery(id+"F0.wireOp",EDGE,"E23");var subQ17=sQuery(id+"F0.wireOp",EDGE,"E22");var subQ18=sQuery(id+"F0.wireOp",EDGE,"E21");var subQ19=sQuery(id+"F0.wireOp",EDGE,"E20");var subQ20=sQuery(id+"F0.wireOp",EDGE,"E19");var subQ21=sQuery(id+"F0.wireOp",EDGE,"E18");var subQ22=sQuery(id+"F0.wireOp",EDGE,"E17");var subQ23=sQuery(id+"F0.wireOp",EDGE,"E16");var subQ24=sQuery(id+"F0.wireOp",EDGE,"E15");var subQ25=sQuery(id+"F0.wireOp",EDGE,"E14");var subQ26=sQuery(id+"F0.wireOp",EDGE,"E13");var subQ27=sQuery(id+"F0.wireOp",EDGE,"E12");var subQ28=sQuery(id+"F0.wireOp",EDGE,"E11");var subQ29=sQuery(id+"F0.wireOp",EDGE,"E10");var subQ30=sQuery(id+"F0.wireOp",EDGE,"E9");var subQ31=sQuery(id+"F0.wireOp",EDGE,"E8");var subQ32=sQuery(id+"F0.wireOp",EDGE,"E7");var subQ33=sQuery(id+"F0.wireOp",EDGE,"E6");var subQ34=sQuery(id+"F0.wireOp",EDGE,"E5");var subQ35=sQuery(id+"F0.wireOp",EDGE,"E4");var subQ36=sQuery(id+"F0.wireOp",EDGE,"E3");var subQ37=sQuery(id+"F0.wireOp",EDGE,"E2");var subQ38=sQuery(id+"F0.wireOp",EDGE,"E1");var subQ39=sQuery(id+"F0.wireOp",EDGE,"E0");Q9=makeQuery(id+"F2.opShell","OFFSET_FACE",FACE,{"disambiguationData":[OSD([subQ39,subQ38,subQ37,subQ36,subQ35,subQ34,subQ33,subQ32,subQ31,subQ30,subQ29,subQ28,subQ27,subQ26,subQ25,subQ24,subQ23,subQ22,subQ21,subQ20,subQ19,subQ18,subQ17,subQ16,subQ15,subQ14,subQ13,subQ12,subQ11,subQ10,subQ9,subQ8,subQ7,subQ6,subQ5,subQ4,subQ3,subQ2,subQ1,subQ0]),TDD([makeQuery(id+"F1.opExtrude","CAP_FACE",FACE,{"disambiguationData":[OSD([subQ39,subQ38,subQ37,subQ36,subQ35,subQ34,subQ33,subQ32,subQ31,subQ30,subQ29,subQ28,subQ27,subQ26,subQ25,subQ24,subQ23,subQ22,subQ21,subQ20,subQ19,subQ18,subQ17,subQ16,subQ15,subQ14,subQ13,subQ12,subQ11,subQ10,subQ9,subQ8,subQ7,subQ6,subQ5,subQ4,subQ3,subQ2,subQ1,subQ0])],"isStart":false})]),OD(2.0)]});}
            var Q10;
            {var subQ0=sQuery(id+"F0.wireOp",EDGE,"E39");var subQ1=sQuery(id+"F0.wireOp",EDGE,"E38");var subQ2=sQuery(id+"F0.wireOp",EDGE,"E37");var subQ3=sQuery(id+"F0.wireOp",EDGE,"E36");var subQ4=sQuery(id+"F0.wireOp",EDGE,"E35");var subQ5=sQuery(id+"F0.wireOp",EDGE,"E34");var subQ6=sQuery(id+"F0.wireOp",EDGE,"E33");var subQ7=sQuery(id+"F0.wireOp",EDGE,"E32");var subQ8=sQuery(id+"F0.wireOp",EDGE,"E31");var subQ9=sQuery(id+"F0.wireOp",EDGE,"E30");var subQ10=sQuery(id+"F0.wireOp",EDGE,"E29");var subQ11=sQuery(id+"F0.wireOp",EDGE,"E28");var subQ12=sQuery(id+"F0.wireOp",EDGE,"E27");var subQ13=sQuery(id+"F0.wireOp",EDGE,"E26");var subQ14=sQuery(id+"F0.wireOp",EDGE,"E25");var subQ15=sQuery(id+"F0.wireOp",EDGE,"E24");var subQ16=sQuery(id+"F0.wireOp",EDGE,"E23");var subQ17=sQuery(id+"F0.wireOp",EDGE,"E22");var subQ18=sQuery(id+"F0.wireOp",EDGE,"E21");var subQ19=sQuery(id+"F0.wireOp",EDGE,"E20");var subQ20=sQuery(id+"F0.wireOp",EDGE,"E19");var subQ21=sQuery(id+"F0.wireOp",EDGE,"E18");var subQ22=sQuery(id+"F0.wireOp",EDGE,"E17");var subQ23=sQuery(id+"F0.wireOp",EDGE,"E16");var subQ24=sQuery(id+"F0.wireOp",EDGE,"E15");var subQ25=sQuery(id+"F0.wireOp",EDGE,"E14");var subQ26=sQuery(id+"F0.wireOp",EDGE,"E13");var subQ27=sQuery(id+"F0.wireOp",EDGE,"E12");var subQ28=sQuery(id+"F0.wireOp",EDGE,"E11");var subQ29=sQuery(id+"F0.wireOp",EDGE,"E10");var subQ30=sQuery(id+"F0.wireOp",EDGE,"E9");var subQ31=sQuery(id+"F0.wireOp",EDGE,"E8");var subQ32=sQuery(id+"F0.wireOp",EDGE,"E7");var subQ33=sQuery(id+"F0.wireOp",EDGE,"E6");var subQ34=sQuery(id+"F0.wireOp",EDGE,"E5");var subQ35=sQuery(id+"F0.wireOp",EDGE,"E4");var subQ36=sQuery(id+"F0.wireOp",EDGE,"E3");var subQ37=sQuery(id+"F0.wireOp",EDGE,"E2");var subQ38=sQuery(id+"F0.wireOp",EDGE,"E1");var subQ39=sQuery(id+"F0.wireOp",EDGE,"E0");Q10=makeQuery(id+"F2.opShell","OFFSET_FACE",FACE,{"disambiguationData":[OSD([subQ39,subQ38,subQ37,subQ36,subQ35,subQ34,subQ33,subQ32,subQ31,subQ30,subQ29,subQ28,subQ27,subQ26,subQ25,subQ24,subQ23,subQ22,subQ21,subQ20,subQ19,subQ18,subQ17,subQ16,subQ15,subQ14,subQ13,subQ12,subQ11,subQ10,subQ9,subQ8,subQ7,subQ6,subQ5,subQ4,subQ3,subQ2,subQ1,subQ0]),TDD([makeQuery(id+"F1.opExtrude","CAP_FACE",FACE,{"disambiguationData":[OSD([subQ39,subQ38,subQ37,subQ36,subQ35,subQ34,subQ33,subQ32,subQ31,subQ30,subQ29,subQ28,subQ27,subQ26,subQ25,subQ24,subQ23,subQ22,subQ21,subQ20,subQ19,subQ18,subQ17,subQ16,subQ15,subQ14,subQ13,subQ12,subQ11,subQ10,subQ9,subQ8,subQ7,subQ6,subQ5,subQ4,subQ3,subQ2,subQ1,subQ0])],"isStart":false})]),OD(6.0)]});}
            extrude(context, id + "F3", {"entities" : qUnion([Q0, Q1, Q2, Q3, Q4, Q5, Q6, Q7, Q8, Q9, Q10]), "operationType" : NewBodyOperationType.REMOVE, "oppositeDirection" : true, "depth" : 12.6 * mm});
        }
    });
